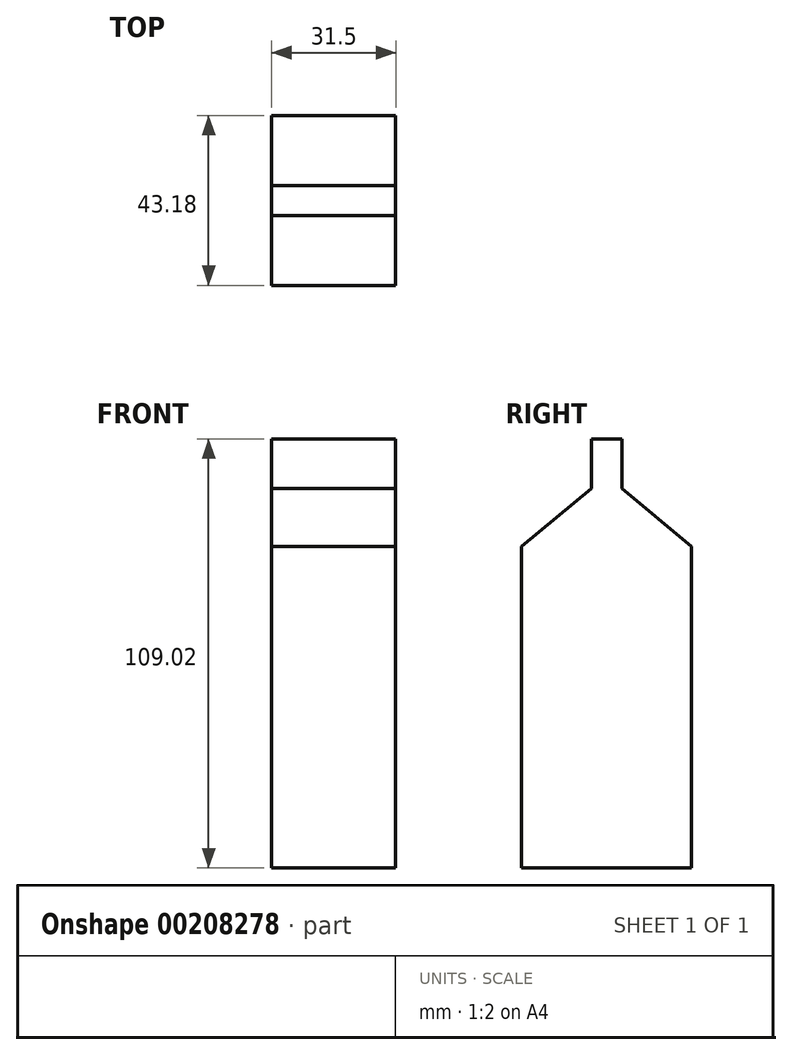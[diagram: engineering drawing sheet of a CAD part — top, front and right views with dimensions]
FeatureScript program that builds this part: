
annotation { "Feature Type Name" : "Feature", "Feature Type Description" : "" }
export const myFeature = defineFeature(function(context is Context, id is Id, definition is map)
    precondition{}
    {
        {
            var Q0;
            Q0=qCreatedBy(makeId("Right.planeOp"),FACE);
            var sketch = newSketch(context, id + "F0", { "sketchPlane" : qUnion([Q0])});
            skLineSegment(sketch, "E0.top", {"start": v(21.6, -40.86) * mm, "end": v(-21.6, -40.86) * mm});
            skLineSegment(sketch, "E0.left", {"start": v(21.6, 40.86) * mm, "end": v(21.6, -40.86) * mm});
            skLineSegment(sketch, "E0.right", {"start": v(-21.6, 40.86) * mm, "end": v(-21.6, -40.86) * mm});
            skPoint(sketch, "E0.middle", {"position": v(0, 0) * mm});
            skLineSegment(sketch, "E1", {"start": v(21.6, 40.86) * mm, "end": v(3.83, 55.6) * mm});
            skLineSegment(sketch, "E2", {"start": v(3.83, 55.6) * mm, "end": v(3.83, 68.16) * mm});
            skLineSegment(sketch, "E3", {"start": v(3.83, 68.16) * mm, "end": v(0, 68.16) * mm});
            skLineSegment(sketch, "E4.MirrorCS", {"start": v(-3.83, 68.16) * mm, "end": v(0, 68.16) * mm});
            skLineSegment(sketch, "E5.MirrorCS", {"start": v(-3.83, 55.6) * mm, "end": v(-3.83, 68.16) * mm});
            skLineSegment(sketch, "E6.MirrorCS", {"start": v(-21.6, 40.86) * mm, "end": v(-3.83, 55.6) * mm});
            skSolve(sketch);
        }
        {
            var Q0;
            Q0=makeQuery(id+"F0.imprint","IMPRINT",FACE,{"disambiguationData":[TD([[makeQuery(id+"F0.imprint","IMPRINT",EDGE,{"derivedFrom":sQuery(id+"F0.wireOp",EDGE,"E0.top")}),-1.0]])]});
            extrude(context, id + "F1", {"entities" : qUnion([Q0]), "endBound" : BoundingType.SYMMETRIC, "depth" : 31.5 * mm});
        }
    });
